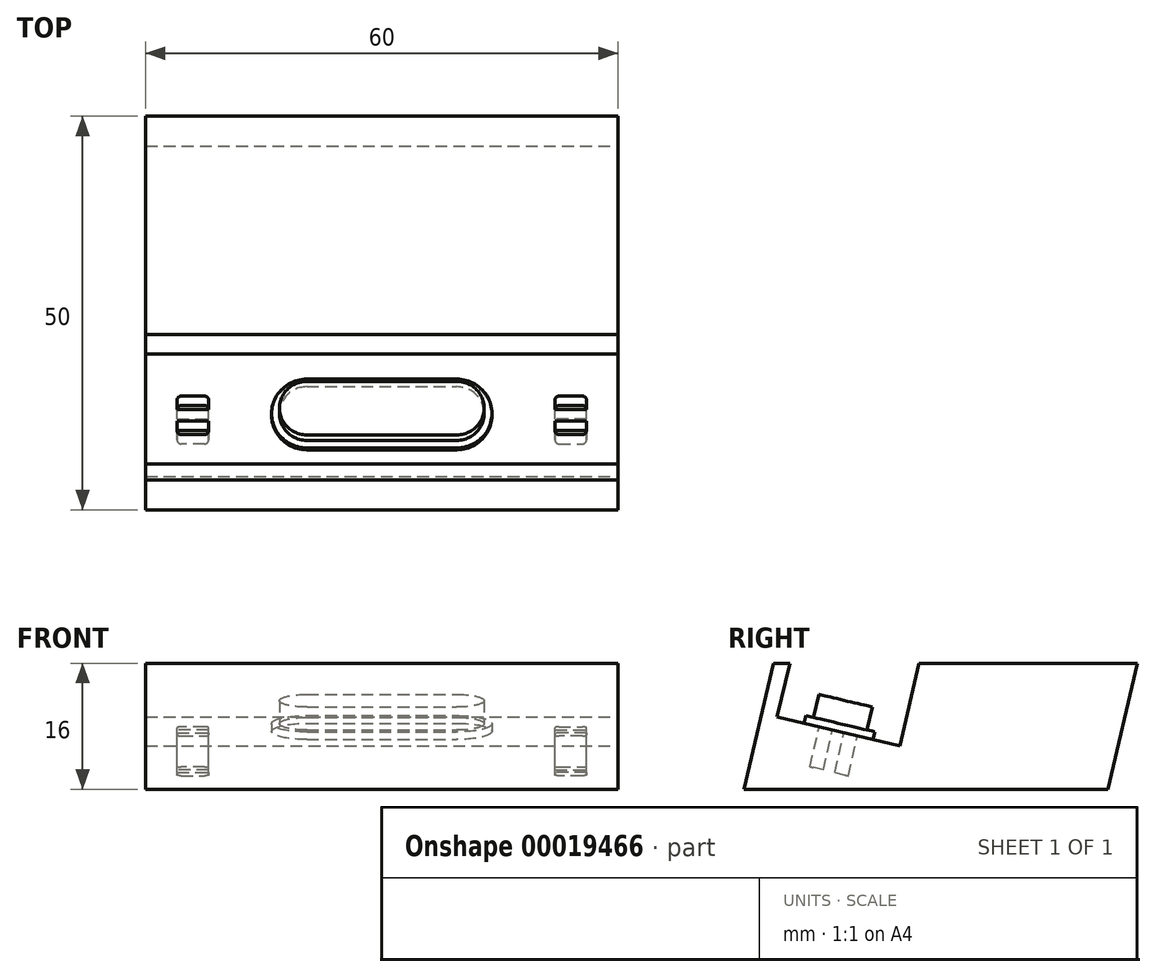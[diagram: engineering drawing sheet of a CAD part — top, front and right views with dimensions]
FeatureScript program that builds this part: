
annotation { "Feature Type Name" : "Feature", "Feature Type Description" : "" }
export const myFeature = defineFeature(function(context is Context, id is Id, definition is map)
    precondition{}
    {
        {
            var Q0;
            Q0=qCreatedBy(makeId("Top.planeOp"),FACE);
            var sketch = newSketch(context, id + "F0", { "sketchPlane" : qUnion([Q0])});
            skLineSegment(sketch, "E0.rect.bottom", {"start": v(30, 25) * mm, "end": v(-30, 25) * mm});
            skLineSegment(sketch, "E0.rect.top", {"start": v(30, -25) * mm, "end": v(-30, -25) * mm});
            skLineSegment(sketch, "E0.rect.left", {"start": v(30, 25) * mm, "end": v(30, -25) * mm});
            skLineSegment(sketch, "E0.rect.right", {"start": v(-30, 25) * mm, "end": v(-30, -25) * mm});
            skPoint(sketch, "E0.rect.middle", {"position": v(0, 0) * mm});
            skSolve(sketch);
        }
        {
            var Q0;
            Q0 = qSketchRegion(id + "F0", true);
            extrude(context, id + "F1", {"entities" : qUnion([Q0]), "depth" : 16 * mm});
        }
        {
            var Q0;
            Q0=makeQuery(id+"F1.opExtrude","SWEPT_FACE",FACE,{"disambiguationData":[OSD([sQuery(id+"F0.wireOp",EDGE,"E0.rect.left")])]});
            var sketch = newSketch(context, id + "F2", { "sketchPlane" : qUnion([Q0])});
            skLineSegment(sketch, "E1", {"start": v(-25, 0) * mm, "end": v(-21.23, 16) * mm});
            skLineSegment(sketch, "E2", {"start": v(25, 16) * mm, "end": v(21.23, 0) * mm});
            skLineSegment(sketch, "E3", {"start": v(-19.18, 16) * mm, "end": v(-20.78, 9.19) * mm});
            skLineSegment(sketch, "E4", {"start": v(-20.78, 9.19) * mm, "end": v(-5.2, 5.52) * mm});
            skLineSegment(sketch, "E5", {"start": v(-5.2, 5.52) * mm, "end": v(-2.74, 16) * mm});
            skSolve(sketch);
        }
        {
            var Q0;
            Q0 = qSketchRegion(id + "F2", true);
            var Q1;
            {var subQ2=sQuery(id+"F2.wireOp",EDGE,"E1");Q1=makeQuery(id+"F2.imprint","IMPRINT",FACE,{"disambiguationData":[TD([[makeQuery(id+"F2.imprint","IMPRINT",EDGE,{"derivedFrom":subQ2}),1.0]])]});}
            var Q2;
            {var subQ2=sQuery(id+"F2.wireOp",EDGE,"E2");Q2=makeQuery(id+"F2.imprint","IMPRINT",FACE,{"disambiguationData":[TD([[makeQuery(id+"F2.imprint","IMPRINT",EDGE,{"derivedFrom":subQ2}),1.0]])]});}
            var Q3;
            {var subQ2=sQuery(id+"F2.wireOp",EDGE,"E3");Q3=makeQuery(id+"F2.imprint","IMPRINT",FACE,{"disambiguationData":[TD([[makeQuery(id+"F2.imprint","IMPRINT",EDGE,{"derivedFrom":subQ2}),1.0]])]});}
            extrude(context, id + "F3", {"entities" : qUnion([Q0, Q1, Q2, Q3]), "operationType" : NewBodyOperationType.REMOVE, "endBound" : BoundingType.THROUGH_ALL, "oppositeDirection" : true, "depth" : 25 * mm});
        }
        {
            var Q0;
            Q0=makeQuery(id+"F3.boolean.opBoolean","COPY",FACE,{"derivedFrom":makeQuery(id+"F3.opExtrude","SWEPT_FACE",FACE,{"disambiguationData":[OSD([sQuery(id+"F2.wireOp",EDGE,"E4")])]})});
            var sketch = newSketch(context, id + "F4", { "sketchPlane" : qUnion([Q0])});
            skLineSegment(sketch, "E6", {"start": v(0, -6.33) * mm, "end": v(0, -22.33) * mm, "construction": true});
            skLineSegment(sketch, "E7", {"start": v(-30, -14.33) * mm, "end": v(30, -14.33) * mm, "construction": true});
            skLineSegment(sketch, "E8", {"start": v(-9.5, -9.83) * mm, "end": v(9.5, -9.83) * mm});
            skLineSegment(sketch, "E9", {"start": v(-9.5, -18.83) * mm, "end": v(9.5, -18.83) * mm});
            skPoint(sketch, "E10", {"position": v(0, -9.83) * mm});
            skPoint(sketch, "E11", {"position": v(0, -18.83) * mm});
            skLineSegment(sketch, "E12", {"start": v(-5.66, -18.83) * mm, "end": v(-5.66, -14.33) * mm, "construction": true});
            skLineSegment(sketch, "E13", {"start": v(-5.66, -14.33) * mm, "end": v(-5.66, -9.83) * mm, "construction": true});
            skArc(sketch, "E14", {"start": v(-9.5, -9.83) * mm, "mid": v(-14, -14.33) * mm, "end": v(-9.5, -18.83) * mm});
            skArc(sketch, "E15", {"start": v(9.5, -18.83) * mm, "mid": v(14, -14.33) * mm, "end": v(9.5, -9.83) * mm});
            skPoint(sketch, "E16", {"position": v(14, -14.33) * mm});
            skPoint(sketch, "E17", {"position": v(-14, -14.33) * mm});
            skPoint(sketch, "E18.orphan", {"position": v(-14, -18.83) * mm});
            skPoint(sketch, "E19.orphan", {"position": v(14, -18.83) * mm});
            skPoint(sketch, "E20.orphan", {"position": v(14, -9.83) * mm});
            skPoint(sketch, "E21.orphan", {"position": v(-14, -9.83) * mm});
            skSolve(sketch);
        }
        {
            var Q0;
            Q0 = qSketchRegion(id + "F4", true);
            extrude(context, id + "F5", {"entities" : qUnion([Q0]), "operationType" : NewBodyOperationType.ADD, "depth" : 1 * mm});
        }
        {
            var Q0;
            Q0=makeQuery(id+"F3.boolean.opBoolean","COPY",FACE,{"derivedFrom":makeQuery(id+"F3.opExtrude","SWEPT_FACE",FACE,{"disambiguationData":[OSD([sQuery(id+"F2.wireOp",EDGE,"E4")])]})});
            var sketch = newSketch(context, id + "F6", { "sketchPlane" : qUnion([Q0])});
            skLineSegment(sketch, "E22.rect.bottom", {"start": v(26, -13.58) * mm, "end": v(22, -13.58) * mm});
            skLineSegment(sketch, "E22.rect.top", {"start": v(26, -11.83) * mm, "end": v(22, -11.83) * mm});
            skLineSegment(sketch, "E22.rect.left", {"start": v(26, -13.58) * mm, "end": v(26, -11.83) * mm});
            skLineSegment(sketch, "E22.rect.right", {"start": v(22, -13.58) * mm, "end": v(22, -11.83) * mm});
            skPoint(sketch, "E22.rect.middle", {"position": v(24, -12.7) * mm});
            skLineSegment(sketch, "E23.bottom", {"start": v(22, -15.08) * mm, "end": v(26, -15.08) * mm});
            skLineSegment(sketch, "E23.top", {"start": v(22, -16.83) * mm, "end": v(26, -16.83) * mm});
            skLineSegment(sketch, "E23.left", {"start": v(22, -15.08) * mm, "end": v(22, -16.83) * mm});
            skLineSegment(sketch, "E23.right", {"start": v(26, -15.08) * mm, "end": v(26, -16.83) * mm});
            skLineSegment(sketch, "E24.MirrorCS", {"start": v(-26, -13.58) * mm, "end": v(-22, -13.58) * mm});
            skLineSegment(sketch, "E25.MirrorCS", {"start": v(-22, -13.58) * mm, "end": v(-22, -11.83) * mm});
            skLineSegment(sketch, "E26.MirrorCS", {"start": v(-26, -11.83) * mm, "end": v(-22, -11.83) * mm});
            skLineSegment(sketch, "E27.MirrorCS", {"start": v(-26, -13.58) * mm, "end": v(-26, -11.83) * mm});
            skLineSegment(sketch, "E28.MirrorCS", {"start": v(-22, -15.08) * mm, "end": v(-26, -15.08) * mm});
            skLineSegment(sketch, "E29.MirrorCS", {"start": v(-26, -15.08) * mm, "end": v(-26, -16.83) * mm});
            skLineSegment(sketch, "E30.MirrorCS", {"start": v(-22, -16.83) * mm, "end": v(-26, -16.83) * mm});
            skLineSegment(sketch, "E31.MirrorCS", {"start": v(-22, -15.08) * mm, "end": v(-22, -16.83) * mm});
            skSolve(sketch);
        }
        {
            var Q0;
            Q0 = qSketchRegion(id + "F6", true);
            extrude(context, id + "F7", {"entities" : qUnion([Q0]), "operationType" : NewBodyOperationType.REMOVE, "oppositeDirection" : true, "depth" : 5.2 * mm});
        }
        {
            var Q0;
            Q0=makeQuery(id+"F7.boolean.opBoolean","COPY",EDGE,{"derivedFrom":makeQuery(id+"F7.opExtrude","SWEPT_EDGE",EDGE,{"disambiguationData":[OSD([sQuery(id+"F6.wireOp",EDGE,"E29.MirrorCS"),sQuery(id+"F6.wireOp",EDGE,"E30.MirrorCS")])]})});
            var Q1;
            Q1=makeQuery(id+"F7.boolean.opBoolean","COPY",EDGE,{"derivedFrom":makeQuery(id+"F7.opExtrude","SWEPT_EDGE",EDGE,{"disambiguationData":[OSD([sQuery(id+"F6.wireOp",EDGE,"E23.top"),sQuery(id+"F6.wireOp",EDGE,"E23.left")])]})});
            var Q2;
            Q2=makeQuery(id+"F7.boolean.opBoolean","COPY",EDGE,{"derivedFrom":makeQuery(id+"F7.opExtrude","SWEPT_EDGE",EDGE,{"disambiguationData":[OSD([sQuery(id+"F6.wireOp",EDGE,"E23.top"),sQuery(id+"F6.wireOp",EDGE,"E23.right")])]})});
            var Q3;
            Q3=makeQuery(id+"F7.boolean.opBoolean","COPY",EDGE,{"derivedFrom":makeQuery(id+"F7.opExtrude","SWEPT_EDGE",EDGE,{"disambiguationData":[OSD([sQuery(id+"F6.wireOp",EDGE,"E30.MirrorCS"),sQuery(id+"F6.wireOp",EDGE,"E31.MirrorCS")])]})});
            var Q4;
            Q4=makeQuery(id+"F7.boolean.opBoolean","COPY",EDGE,{"derivedFrom":makeQuery(id+"F7.opExtrude","SWEPT_EDGE",EDGE,{"disambiguationData":[OSD([sQuery(id+"F6.wireOp",EDGE,"E25.MirrorCS"),sQuery(id+"F6.wireOp",EDGE,"E26.MirrorCS")])]})});
            var Q5;
            Q5=makeQuery(id+"F7.boolean.opBoolean","COPY",EDGE,{"derivedFrom":makeQuery(id+"F7.opExtrude","SWEPT_EDGE",EDGE,{"disambiguationData":[OSD([sQuery(id+"F6.wireOp",EDGE,"E26.MirrorCS"),sQuery(id+"F6.wireOp",EDGE,"E27.MirrorCS")])]})});
            var Q6;
            Q6=makeQuery(id+"F7.boolean.opBoolean","COPY",EDGE,{"derivedFrom":makeQuery(id+"F7.opExtrude","SWEPT_EDGE",EDGE,{"disambiguationData":[OSD([sQuery(id+"F6.wireOp",EDGE,"E22.rect.top"),sQuery(id+"F6.wireOp",EDGE,"E22.rect.right")])]})});
            var Q7;
            Q7=makeQuery(id+"F7.boolean.opBoolean","COPY",EDGE,{"derivedFrom":makeQuery(id+"F7.opExtrude","SWEPT_EDGE",EDGE,{"disambiguationData":[OSD([sQuery(id+"F6.wireOp",EDGE,"E22.rect.top"),sQuery(id+"F6.wireOp",EDGE,"E22.rect.left")])]})});
            fillet(context, id + "F8", {"entities" : qUnion([Q0, Q1, Q2, Q3, Q4, Q5, Q6, Q7]), "radius" : 0.5 * mm, "tangentPropagation" : true, "allowEdgeOverflow" : false});
        }
        {
            var Q0;
            Q0=makeQuery(id+"F5.opExtrude","CAP_FACE",FACE,{"disambiguationData":[OSD([sQuery(id+"F4.wireOp",EDGE,"E8"),sQuery(id+"F4.wireOp",EDGE,"E9"),sQuery(id+"F4.wireOp",EDGE,"E14"),sQuery(id+"F4.wireOp",EDGE,"E15")])],"isStart":false});
            var sketch = newSketch(context, id + "F9", { "sketchPlane" : qUnion([Q0])});
            skArc(sketch, "E32", {"start": v(-9.5, -10.83) * mm, "mid": v(-13, -14.33) * mm, "end": v(-9.5, -17.83) * mm});
            skArc(sketch, "E33", {"start": v(9.5, -17.83) * mm, "mid": v(13, -14.33) * mm, "end": v(9.5, -10.83) * mm});
            skLineSegment(sketch, "E34", {"start": v(-9.5, -10.83) * mm, "end": v(9.5, -10.83) * mm});
            skLineSegment(sketch, "E35", {"start": v(-9.5, -17.83) * mm, "end": v(9.5, -17.83) * mm});
            skSolve(sketch);
        }
        {
            var Q0;
            Q0 = qSketchRegion(id + "F9", true);
            extrude(context, id + "F10", {"entities" : qUnion([Q0]), "operationType" : NewBodyOperationType.ADD, "depth" : 3 * mm});
        }
    });
